# Revit family: Toilet_Seat-Round-DXV-Traditional-5020B15G_Series
name_source: partatom
category: Specialty Equipment
revit_build: Autodesk Revit 2014 (Build: 20130308_1515(x64)
units: mm (PartAtom-declared; Revit-internal decimal feet)

## types (2) — shared parameters
Assembly Code = C1030200
Default Elevation = 0"
Description = DXV Traditional Luxury Toilet Seat
Height = 2 5/16"
Hole Width = 5 1/2"
Installation Type = Surface Mounted
Length = 16 11/16"
Manufacturer = DXV
Price = Prices may vary. Please consult Manufacturer Representative for most up-to-date price list.
Shipping Weight = 4.3 lb
URL = https://www.dxv.com
Width = 14 1/8"

## per-type parameters (varying)
| type | Finish | Material |
| 5020B15G.415 | Plastic-DXV-415-Canvas White | Plastic-DXV-415-Canvas White |
| 5020B15G.071 | Plastic-DXV-071-Biscuit | Plastic-DXV-071-Biscuit |

note: column(s) folded — value = type name in every type: Model

## geometry (parser evidence)
native form markers: Sweep x1
no freeform markers — native parametric forms only
